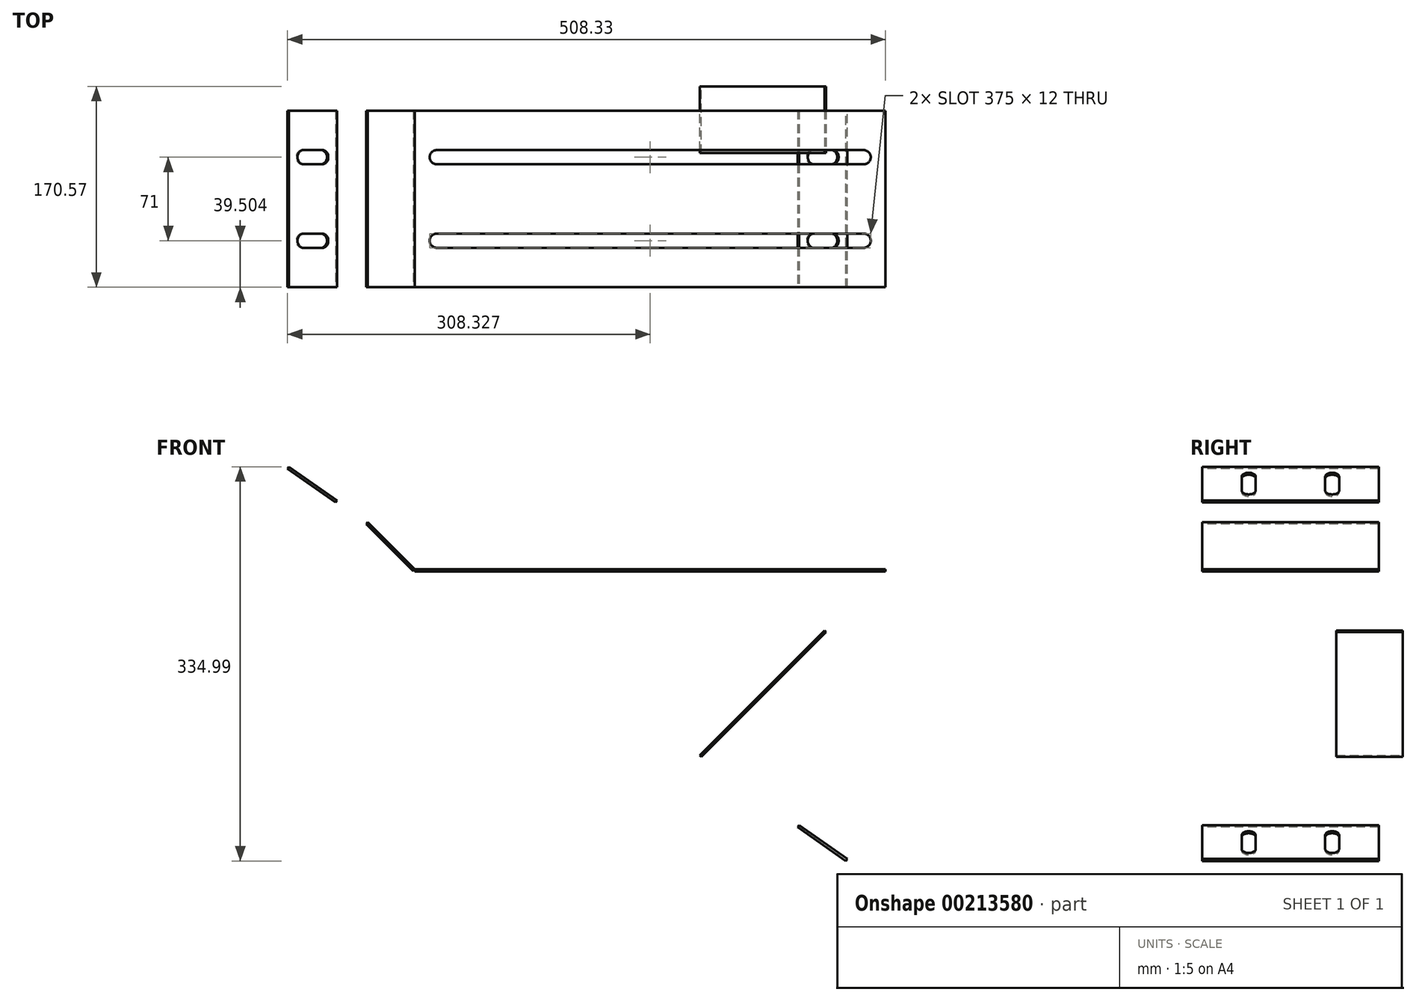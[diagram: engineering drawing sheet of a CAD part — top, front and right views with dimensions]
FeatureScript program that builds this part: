
annotation { "Feature Type Name" : "Feature", "Feature Type Description" : "" }
export const myFeature = defineFeature(function(context is Context, id is Id, definition is map)
    precondition{}
    {
        {
            var Q0;
            Q0=qCreatedBy(makeId("Top.planeOp"),FACE);
            var sketch = newSketch(context, id + "F0", { "sketchPlane" : qUnion([Q0])});
            skLineSegment(sketch, "E0.bottom", {"start": v(-269.46, 129.75) * mm, "end": v(130.54, 129.75) * mm});
            skLineSegment(sketch, "E0.top", {"start": v(-269.46, -20.25) * mm, "end": v(130.54, -20.25) * mm});
            skLineSegment(sketch, "E0.left", {"start": v(-269.46, 129.75) * mm, "end": v(-269.46, -20.25) * mm});
            skLineSegment(sketch, "E0.right", {"start": v(130.54, 129.75) * mm, "end": v(130.54, -20.25) * mm});
            skLineSegment(sketch, "E1", {"start": v(130.54, 54.75) * mm, "end": v(-269.46, 54.75) * mm, "construction": true});
            skLineSegment(sketch, "E2", {"start": v(-69.46, 129.75) * mm, "end": v(-69.46, -20.25) * mm, "construction": true});
            skLineSegment(sketch, "E3.bottom", {"start": v(118.04, 25.25) * mm, "end": v(-256.96, 25.25) * mm});
            skLineSegment(sketch, "E3.top", {"start": v(118.04, 13.25) * mm, "end": v(-256.96, 13.25) * mm});
            skLineSegment(sketch, "E3.left", {"start": v(118.04, 25.25) * mm, "end": v(118.04, 13.25) * mm, "construction": true});
            skLineSegment(sketch, "E3.right", {"start": v(-256.96, 25.25) * mm, "end": v(-256.96, 13.25) * mm, "construction": true});
            skArc(sketch, "E4", {"start": v(112.04, 13.25) * mm, "mid": v(118.04, 19.25) * mm, "end": v(112.04, 25.25) * mm});
            skArc(sketch, "E5", {"start": v(-250.96, 25.25) * mm, "mid": v(-256.96, 19.25) * mm, "end": v(-250.96, 13.25) * mm});
            skLineSegment(sketch, "E6", {"start": v(112.04, 96.25) * mm, "end": v(-250.96, 96.25) * mm});
            skLineSegment(sketch, "E7", {"start": v(112.04, 84.25) * mm, "end": v(-250.96, 84.25) * mm});
            skArc(sketch, "E8", {"start": v(112.04, 84.25) * mm, "mid": v(118.04, 90.25) * mm, "end": v(112.04, 96.25) * mm});
            skArc(sketch, "E9", {"start": v(-250.96, 96.25) * mm, "mid": v(-256.96, 90.25) * mm, "end": v(-250.96, 84.25) * mm});
            skSolve(sketch);
        }
        {
            var Q0;
            Q0=makeQuery(id+"F0.imprint","IMPRINT",FACE,{"disambiguationData":[TD([[makeQuery(id+"F0.imprint","IMPRINT",EDGE,{"derivedFrom":sQuery(id+"F0.wireOp",EDGE,"E0.bottom")}),-1.0]])]});
            extrude(context, id + "F1", {"entities" : qUnion([Q0]), "depth" : 2 * mm});
        }
        {
            var Q0;
            Q0=makeQuery(id+"F1.opExtrude","CAP_FACE",FACE,{"disambiguationData":[OSD([sQuery(id+"F0.wireOp",EDGE,"E0.bottom"),sQuery(id+"F0.wireOp",EDGE,"E0.top"),sQuery(id+"F0.wireOp",EDGE,"E0.left"),sQuery(id+"F0.wireOp",EDGE,"E0.right"),sQuery(id+"F0.wireOp",EDGE,"E3.bottom"),sQuery(id+"F0.wireOp",EDGE,"E3.top"),sQuery(id+"F0.wireOp",EDGE,"E4"),sQuery(id+"F0.wireOp",EDGE,"E5"),sQuery(id+"F0.wireOp",EDGE,"E6"),sQuery(id+"F0.wireOp",EDGE,"E7"),sQuery(id+"F0.wireOp",EDGE,"E8"),sQuery(id+"F0.wireOp",EDGE,"E9")])],"isStart":false});
            var Q1;
            Q1=makeQuery(id+"F1.opExtrude","CAP_EDGE",EDGE,{"disambiguationData":[OSD([sQuery(id+"F0.wireOp",EDGE,"E0.right")])],"isStart":false});
            cPlane(context, id + "F2", {"entities" : qUnion([Q0, Q1]), "cplaneType" : CPlaneType.LINE_ANGLE, "offset" : 25 * mm, "angle" : 45 * degree, "width" : 150 * mm, "height" : 150 * mm});
        }
        {
            var Q0;
            Q0=qCreatedBy(id+"F2.planeOp",FACE);
            var sketch = newSketch(context, id + "F3", { "sketchPlane" : qUnion([Q0])});
            skLineSegment(sketch, "E10.0", {"start": v(93.72, -129.75) * mm, "end": v(93.72, 20.25) * mm});
            skLineSegment(sketch, "E11", {"start": v(93.72, -129.75) * mm, "end": v(150.32, -129.75) * mm});
            skLineSegment(sketch, "E12", {"start": v(150.32, -129.75) * mm, "end": v(150.32, 20.25) * mm});
            skLineSegment(sketch, "E13", {"start": v(150.32, 20.25) * mm, "end": v(93.72, 20.25) * mm});
            skLineSegment(sketch, "E14", {"start": v(93.72, -54.75) * mm, "end": v(150.32, -54.75) * mm, "construction": true});
            skSolve(sketch);
        }
        {
            var Q0;
            Q0=makeQuery(id+"F3.imprint","IMPRINT",FACE,{"disambiguationData":[TD([[makeQuery(id+"F3.imprint","IMPRINT",EDGE,{"derivedFrom":sQuery(id+"F3.wireOp",EDGE,"E10.0")}),-1.0]])]});
            extrude(context, id + "F4", {"entities" : qUnion([Q0]), "depth" : 2 * mm});
        }
        {
            var Q0;
            Q0=makeQuery(id+"F4.opExtrude","SWEPT_BODY",BODY,{"disambiguationData":[OSD([sQuery(id+"F3.wireOp",EDGE,"E10.0"),sQuery(id+"F3.wireOp",EDGE,"E11"),sQuery(id+"F3.wireOp",EDGE,"E12"),sQuery(id+"F3.wireOp",EDGE,"E13")])]});
            var Q1;
            Q1=makeQuery(id+"F1.opExtrude","CAP_EDGE",EDGE,{"disambiguationData":[OSD([sQuery(id+"F0.wireOp",EDGE,"E0.left")])],"isStart":false});
            transform(context, id + "F5", {"entities" : qUnion([Q0]), "transformType" : TransformType.ROTATION, "transformAxis" : qUnion([Q1]), "angle" : 30 * degree, "makeCopy" : true});
        }
        {
            var Q0;
            Q0=makeQuery(id+"F5.opPattern","COPY",BODY,{"derivedFrom":makeQuery(id+"F4.opExtrude","SWEPT_BODY",BODY,{"disambiguationData":[OSD([sQuery(id+"F3.wireOp",EDGE,"E10.0"),sQuery(id+"F3.wireOp",EDGE,"E11"),sQuery(id+"F3.wireOp",EDGE,"E12"),sQuery(id+"F3.wireOp",EDGE,"E13")])]}),"instanceName":"1"});
            deleteBodies(context, id + "F6", {"entities" : qUnion([Q0])});
        }
        {
            var Q0;
            Q0=makeQuery(id+"F1.opExtrude","CAP_FACE",FACE,{"disambiguationData":[OSD([sQuery(id+"F0.wireOp",EDGE,"E0.bottom"),sQuery(id+"F0.wireOp",EDGE,"E0.top"),sQuery(id+"F0.wireOp",EDGE,"E0.left"),sQuery(id+"F0.wireOp",EDGE,"E0.right"),sQuery(id+"F0.wireOp",EDGE,"E3.bottom"),sQuery(id+"F0.wireOp",EDGE,"E3.top"),sQuery(id+"F0.wireOp",EDGE,"E4"),sQuery(id+"F0.wireOp",EDGE,"E5"),sQuery(id+"F0.wireOp",EDGE,"E6"),sQuery(id+"F0.wireOp",EDGE,"E7"),sQuery(id+"F0.wireOp",EDGE,"E8"),sQuery(id+"F0.wireOp",EDGE,"E9")])],"isStart":false});
            var Q1;
            Q1=makeQuery(id+"F1.opExtrude","CAP_EDGE",EDGE,{"disambiguationData":[OSD([sQuery(id+"F0.wireOp",EDGE,"E0.left")])],"isStart":false});
            cPlane(context, id + "F7", {"entities" : qUnion([Q0, Q1]), "cplaneType" : CPlaneType.LINE_ANGLE, "offset" : 25 * mm, "angle" : 135 * degree, "width" : 150 * mm, "height" : 150 * mm});
        }
        {
            var Q0;
            Q0=qCreatedBy(id+"F7.planeOp",FACE);
            var sketch = newSketch(context, id + "F8", { "sketchPlane" : qUnion([Q0])});
            skLineSegment(sketch, "E15.0", {"start": v(129.75, 191.95) * mm, "end": v(-20.25, 191.95) * mm});
            skLineSegment(sketch, "E16", {"start": v(129.75, 191.95) * mm, "end": v(129.75, 248.55) * mm});
            skLineSegment(sketch, "E17", {"start": v(129.75, 248.55) * mm, "end": v(-20.25, 248.55) * mm});
            skLineSegment(sketch, "E18", {"start": v(-20.25, 248.55) * mm, "end": v(-20.25, 191.95) * mm});
            skLineSegment(sketch, "E19", {"start": v(54.75, 191.95) * mm, "end": v(54.75, 248.55) * mm, "construction": true});
            skSolve(sketch);
        }
        {
            var Q0;
            Q0=makeQuery(id+"F8.imprint","IMPRINT",FACE,{"disambiguationData":[TD([[makeQuery(id+"F8.imprint","IMPRINT",EDGE,{"derivedFrom":sQuery(id+"F8.wireOp",EDGE,"E15.0")}),-1.0]])]});
            extrude(context, id + "F9", {"entities" : qUnion([Q0]), "oppositeDirection" : true, "depth" : 2 * mm});
        }
        {
            var Q0;
            Q0=makeQuery(id+"F9.opExtrude","CAP_VERTEX",VERTEX,{"disambiguationData":[OSD([sQuery(id+"F8.wireOp",EDGE,"E17"),sQuery(id+"F8.wireOp",EDGE,"E18")])],"isStart":true});
            var Q1;
            Q1=makeQuery(id+"F9.opExtrude","CAP_VERTEX",VERTEX,{"disambiguationData":[OSD([sQuery(id+"F8.wireOp",EDGE,"E16"),sQuery(id+"F8.wireOp",EDGE,"E17")])],"isStart":true});
            var Q2;
            Q2=makeQuery(id+"F4.opExtrude","CAP_VERTEX",VERTEX,{"disambiguationData":[OSD([sQuery(id+"F3.wireOp",EDGE,"E11"),sQuery(id+"F3.wireOp",EDGE,"E12")])],"isStart":true});
            cPlane(context, id + "F10", {"entities" : qUnion([Q0, Q1, Q2]), "cplaneType" : CPlaneType.THREE_POINT, "offset" : 0 * mm, "width" : 150 * mm, "height" : 150 * mm});
        }
        {
            var Q0;
            Q0=qCreatedBy(id+"F10.planeOp",FACE);
            var sketch = newSketch(context, id + "F11", { "sketchPlane" : qUnion([Q0])});
            skLineSegment(sketch, "E20.0", {"start": v(170.56, 129.75) * mm, "end": v(170.56, -20.25) * mm});
            skLineSegment(sketch, "E20.1", {"start": v(-309.48, 129.75) * mm, "end": v(-309.48, -20.25) * mm});
            skLineSegment(sketch, "E21", {"start": v(-309.48, 129.75) * mm, "end": v(-359.48, 129.75) * mm});
            skLineSegment(sketch, "E22", {"start": v(-359.48, 129.75) * mm, "end": v(-359.48, -20.25) * mm});
            skLineSegment(sketch, "E23", {"start": v(-359.48, -20.25) * mm, "end": v(-309.48, -20.25) * mm});
            skLineSegment(sketch, "E24", {"start": v(-309.48, 54.75) * mm, "end": v(-359.48, 54.75) * mm, "construction": true});
            skArc(sketch, "E25", {"start": v(-324.48, 13.25) * mm, "mid": v(-318.48, 19.25) * mm, "end": v(-324.48, 25.25) * mm});
            skLineSegment(sketch, "E26", {"start": v(-324.48, 13.25) * mm, "end": v(-344.48, 13.25) * mm});
            skLineSegment(sketch, "E27", {"start": v(-324.48, 25.25) * mm, "end": v(-344.48, 25.25) * mm});
            skArc(sketch, "E28", {"start": v(-344.48, 25.25) * mm, "mid": v(-350.48, 19.25) * mm, "end": v(-344.48, 13.25) * mm});
            skArc(sketch, "E29", {"start": v(-324.48, 84.25) * mm, "mid": v(-318.48, 90.25) * mm, "end": v(-324.48, 96.25) * mm});
            skLineSegment(sketch, "E30", {"start": v(-324.48, 84.25) * mm, "end": v(-344.48, 84.25) * mm});
            skLineSegment(sketch, "E31", {"start": v(-324.48, 96.25) * mm, "end": v(-344.48, 96.25) * mm});
            skArc(sketch, "E32", {"start": v(-344.48, 96.25) * mm, "mid": v(-350.48, 90.25) * mm, "end": v(-344.48, 84.25) * mm});
            skLineSegment(sketch, "E33", {"start": v(170.56, 54.75) * mm, "end": v(-309.48, 54.75) * mm, "construction": true});
            skLineSegment(sketch, "E34", {"start": v(-69.46, 54.75) * mm, "end": v(-69.46, 219) * mm, "construction": true});
            skLineSegment(sketch, "E35", {"start": v(170.56, -20.25) * mm, "end": v(220.56, -20.25) * mm});
            skLineSegment(sketch, "E36", {"start": v(220.56, -20.25) * mm, "end": v(220.56, 129.75) * mm});
            skLineSegment(sketch, "E37", {"start": v(220.56, 129.75) * mm, "end": v(170.56, 129.75) * mm});
            skArc(sketch, "E38", {"start": v(205.56, 13.25) * mm, "mid": v(211.56, 19.25) * mm, "end": v(205.56, 25.25) * mm});
            skLineSegment(sketch, "E39", {"start": v(205.56, 13.25) * mm, "end": v(185.56, 13.25) * mm});
            skLineSegment(sketch, "E40", {"start": v(205.56, 25.25) * mm, "end": v(185.56, 25.25) * mm});
            skArc(sketch, "E41", {"start": v(185.56, 25.25) * mm, "mid": v(179.56, 19.25) * mm, "end": v(185.56, 13.25) * mm});
            skArc(sketch, "E42", {"start": v(205.56, 84.25) * mm, "mid": v(211.56, 90.25) * mm, "end": v(205.56, 96.25) * mm});
            skLineSegment(sketch, "E43", {"start": v(205.56, 84.25) * mm, "end": v(185.56, 84.25) * mm});
            skLineSegment(sketch, "E44", {"start": v(205.56, 96.25) * mm, "end": v(185.56, 96.25) * mm});
            skArc(sketch, "E45", {"start": v(185.56, 96.25) * mm, "mid": v(179.56, 90.25) * mm, "end": v(185.56, 84.25) * mm});
            skSolve(sketch);
        }
        {
            var Q0;
            Q0=makeQuery(id+"F11.imprint","IMPRINT",FACE,{"disambiguationData":[TD([[makeQuery(id+"F11.imprint","IMPRINT",EDGE,{"derivedFrom":sQuery(id+"F11.wireOp",EDGE,"E20.1")}),-1.0]])]});
            extrude(context, id + "F12", {"entities" : qUnion([Q0]), "operationType" : NewBodyOperationType.ADD, "oppositeDirection" : true, "depth" : 2 * mm});
        }
        {
            var Q0;
            Q0=makeQuery(id+"F11.imprint","IMPRINT",FACE,{"disambiguationData":[TD([[makeQuery(id+"F11.imprint","IMPRINT",EDGE,{"derivedFrom":sQuery(id+"F11.wireOp",EDGE,"E20.0")}),1.0]])]});
            extrude(context, id + "F13", {"entities" : qUnion([Q0]), "operationType" : NewBodyOperationType.ADD, "oppositeDirection" : true, "depth" : 2 * mm});
        }
    });
